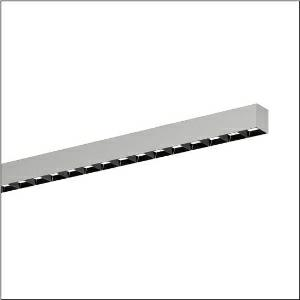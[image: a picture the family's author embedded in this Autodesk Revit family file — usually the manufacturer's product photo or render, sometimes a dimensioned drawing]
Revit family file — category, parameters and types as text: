
# Revit family: silica_21_51mx24dc3asb
name_source: partatom
category: Lighting Fixtures
units: mm (PartAtom-declared; Revit-internal decimal feet)

## family parameters
Cut with Voids When Loaded = No
Host = Face
Light Source = No
Part Type = Normal
Room Calculation Point = No
Round Connector Dimension = Use Diameter
Shared = No

## types (1)
- --- (1 x LED, 10800 lm, 79 W, 3000K)
    Apparent Load = 79 VA
    CIE Flux Codes = 74 94 99 100 100
    Color Rendering = 80
    Color Temperature = 3000K
    Default Elevation = 1800 mm
    Description = Silica 21, office luminaire, primary light control with darklight reflector, of PMMA, black, CAT 2 (L<= 3000cd/m²), light emission: direct distribution, primary light characteristic: asymmetric, installation type: surface-mounted, LED, rated luminous flux: 10.800lm, luminous efficacy: 137lm/W, light colour: 830, colour temperature: 3000K, control gear: DALI 2, with terminal, 3+2-pole, max. 2.5mm², mains connection: 220..240V, AC, 50/60Hz, rated input power: 79W, luminaire housing, of aluminium, metallic grey (RAL 9006), length: 3.004mm, width: 53mm, height: 53mm, protection rating (complete): IP20, insulation class (complete): insulation class I (protective earthing), certification: CE, permissible operating ambient temperature: 0..+35°C, standard: EN 50419, packaging unit: 1 piece
    Height = 53 mm
    Lamp = 1 x LED
    Lamp Light Flux = 10800 lm
    Lamp Power = 79 W
    Lamp count = 1
    Length = 3004 mm
    Luminous efficacy = 137 lm/W
    Manufacturer = Siteco
    ModVariant = No
    Model = 51MX24DC3ASB
    Mounting Place = Ceiling
    Mounting Type = Surface mounted
    Number of Poles = 1
    OnlyDefault = Yes
    Power Factor = 1
    Product Name = Silica 21
    Product group = office luminaire | ceiling mounted
    ProductGroupID = 301
    Protection Class = Protection class I
    Protection Degree = IP 20
    RLX_Detail_Level = 1
    RLX_Emergency_Light_Flux = 0 lm
    RLX_Emergency_Type = 0
    RLX_Emergency_Type_DB = No
    RlxData = <blob elided: 63161 chars, md5=8fb0f94c>
    Socket = socket
    Standby Power = 0 W
    System Light Flux = 10800 lm
    System Power = 79 W
    Type Comments = factory setting: luminous flux: 100 % | dim-lin: 254 | 448 mA
    Type Image = l_1335929.jpg
    URL = http://relux.com
    VarID = @adj_122739
    Voltage = 0 V
    Weight = 0.00 kg
    Width = 53 mm

## geometry (parser evidence)
native form markers: Blend x4, Sweep x10
no freeform markers — native parametric forms only
